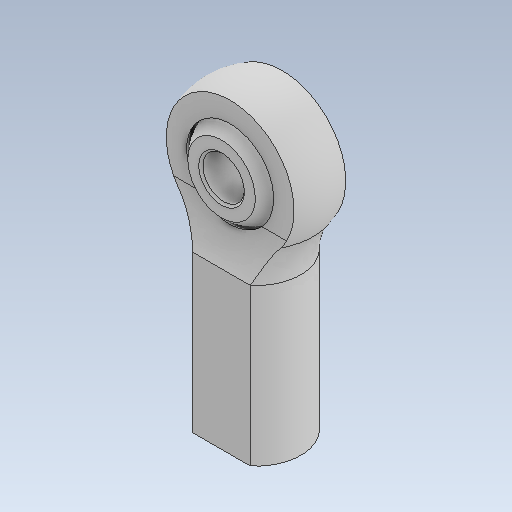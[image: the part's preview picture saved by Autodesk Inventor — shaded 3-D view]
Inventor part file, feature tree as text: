
AUTODESK INVENTOR PART (.ipt)
format: ipt  version: 2023 (Build 270158000, 158)  size: 493,568 bytes
history: native  units: in
note: dims shown in document units (in); Inventor stores cm internally (conversion verified against a paired STEP export)
features: fillet x1, chamfer x1
ambient origin geometry x8: Origin, YZ Plane, XZ Plane, XY Plane, X Axis, Y Axis, Z Axis, Center Point
bodies: Solid1 (feature_tree), Solid2 (feature_tree)
feature tree (2):
  fillet  "Fillet1"  [1 undecoded]
  chamfer  "Chamfer1"  [1 undecoded]
note: 2 required parameter values undecoded (feature->parameter linkage not recoverable at this tier; creation-order binding heuristic only, values carry confidence <= 0.55)
